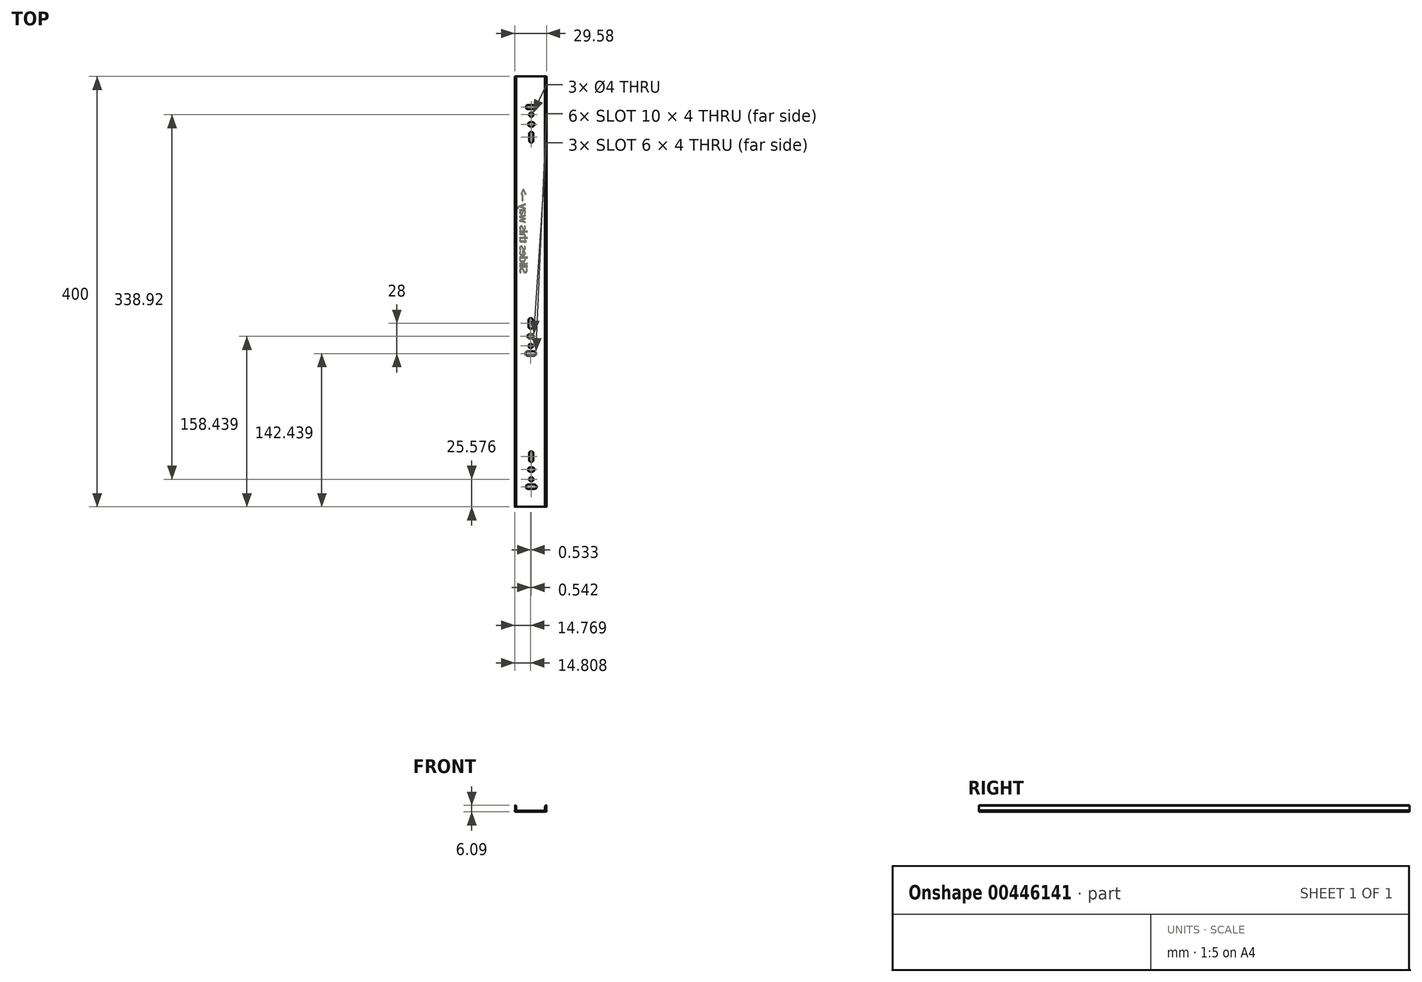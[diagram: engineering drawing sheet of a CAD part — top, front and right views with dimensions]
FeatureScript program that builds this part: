
annotation { "Feature Type Name" : "Feature", "Feature Type Description" : "" }
export const myFeature = defineFeature(function(context is Context, id is Id, definition is map)
    precondition{}
    {
        {
            var Q0;
            Q0=qCreatedBy(makeId("Front.planeOp"),FACE);
            var sketch = newSketch(context, id + "F0", { "sketchPlane" : qUnion([Q0])});
            skArc(sketch, "E0.filletArc", {"start": v(-14.79, 7.2) * mm, "mid": v(-14.47, 6.31) * mm, "end": v(-13.6, 5.94) * mm});
            skFitSpline(sketch, "E1", {"points": [v(-14.73, 11.64) * mm, v(-14.79, 7.2) * mm], "startDerivative": vector(1.38, -3.33) * mm, "endDerivative": vector(-2.04, -4.37) * mm});
            skFitSpline(sketch, "E2.MirrorCS", {"points": [v(14.73, 11.64) * mm, v(14.79, 7.2) * mm], "startDerivative": vector(-1.38, -3.33) * mm, "endDerivative": vector(2.04, -4.37) * mm});
            skArc(sketch, "E3.MirrorCS", {"start": v(14.79, 7.2) * mm, "mid": v(14.47, 6.31) * mm, "end": v(13.6, 5.94) * mm});
            skArc(sketch, "E4.1", {"start": v(-13.77, 7.04) * mm, "mid": v(-13.7, 6.97) * mm, "end": v(-13.6, 6.94) * mm});
            skFitSpline(sketch, "E4.2", {"points": [v(-13.8, 12.03) * mm, v(-13.66, 11.68) * mm, v(-13.43, 10.9) * mm, v(-13.29, 9.58) * mm, v(-13.39, 8.17) * mm, v(-13.67, 7.23) * mm, v(-13.88, 6.77) * mm]});
            skArc(sketch, "E5.1", {"start": v(13.77, 7.04) * mm, "mid": v(13.7, 6.97) * mm, "end": v(13.6, 6.94) * mm});
            skFitSpline(sketch, "E5.2", {"points": [v(13.8, 12.03) * mm, v(13.66, 11.68) * mm, v(13.43, 10.9) * mm, v(13.29, 9.58) * mm, v(13.39, 8.17) * mm, v(13.67, 7.23) * mm, v(13.88, 6.77) * mm]});
            skLineSegment(sketch, "E6", {"start": v(-13.8, 12.03) * mm, "end": v(-14.73, 11.64) * mm});
            skLineSegment(sketch, "E7", {"start": v(13.8, 12.03) * mm, "end": v(14.73, 11.64) * mm});
            skLineSegment(sketch, "E8", {"start": v(-13.6, 6.94) * mm, "end": v(13.6, 6.94) * mm});
            skLineSegment(sketch, "E9", {"start": v(13.6, 5.94) * mm, "end": v(-13.6, 5.94) * mm});
            skSolve(sketch);
        }
        {
            var Q0;
            Q0=makeQuery(id+"F0.imprint","IMPRINT",FACE,{"disambiguationData":[TD([[makeQuery(id+"F0.imprint","IMPRINT",EDGE,{"derivedFrom":sQuery(id+"F0.wireOp",EDGE,"E0.filletArc")}),1.0]])]});
            extrude(context, id + "F1", {"entities" : qUnion([Q0]), "endBound" : BoundingType.SYMMETRIC, "depth" : 400 * mm});
        }
        {
            var Q0;
            Q0=qCreatedBy(makeId("Top.planeOp"),FACE);
            var sketch = newSketch(context, id + "F2", { "sketchPlane" : qUnion([Q0])});
            skLineSegment(sketch, "E10.bottom", {"start": v(3.52, -183.42) * mm, "end": v(-2.48, -183.42) * mm});
            skLineSegment(sketch, "E10.top", {"start": v(3.52, -179.42) * mm, "end": v(-2.48, -179.42) * mm});
            skLineSegment(sketch, "E11.bottom", {"start": v(1.52, -167.42) * mm, "end": v(-0.48, -167.42) * mm});
            skLineSegment(sketch, "E11.top", {"start": v(1.52, -163.42) * mm, "end": v(-0.48, -163.42) * mm});
            skLineSegment(sketch, "E12.left", {"start": v(2.52, -156.42) * mm, "end": v(2.52, -150.42) * mm});
            skLineSegment(sketch, "E12.right", {"start": v(-1.48, -156.42) * mm, "end": v(-1.48, -150.42) * mm});
            skPoint(sketch, "E13.visualSharp", {"position": v(5.52, -183.42) * mm});
            skArc(sketch, "E13.filletArc", {"start": v(3.52, -183.42) * mm, "mid": v(4.94, -182.84) * mm, "end": v(5.52, -181.42) * mm});
            skPoint(sketch, "E14.visualSharp", {"position": v(5.52, -179.42) * mm});
            skArc(sketch, "E14.filletArc", {"start": v(5.52, -181.42) * mm, "mid": v(4.94, -180) * mm, "end": v(3.52, -179.42) * mm});
            skPoint(sketch, "E15.visualSharp", {"position": v(-4.48, -183.42) * mm});
            skArc(sketch, "E15.filletArc", {"start": v(-4.48, -181.42) * mm, "mid": v(-3.9, -182.84) * mm, "end": v(-2.48, -183.42) * mm});
            skPoint(sketch, "E16.visualSharp", {"position": v(-4.48, -179.42) * mm});
            skArc(sketch, "E16.filletArc", {"start": v(-2.48, -179.42) * mm, "mid": v(-3.9, -180) * mm, "end": v(-4.48, -181.42) * mm});
            skPoint(sketch, "E17.visualSharp", {"position": v(-1.48, -176.42) * mm});
            skArc(sketch, "E17.filletArc", {"start": v(-1.48, -174.42) * mm, "mid": v(-0.9, -175.84) * mm, "end": v(0.52, -176.42) * mm});
            skPoint(sketch, "E18.visualSharp", {"position": v(2.52, -176.42) * mm});
            skArc(sketch, "E18.filletArc", {"start": v(0.52, -176.42) * mm, "mid": v(1.94, -175.84) * mm, "end": v(2.52, -174.42) * mm});
            skPoint(sketch, "E19.visualSharp", {"position": v(2.52, -172.42) * mm});
            skArc(sketch, "E19.filletArc", {"start": v(2.52, -174.42) * mm, "mid": v(1.94, -173) * mm, "end": v(0.52, -172.42) * mm});
            skPoint(sketch, "E20.visualSharp", {"position": v(-1.48, -172.42) * mm});
            skArc(sketch, "E20.filletArc", {"start": v(0.52, -172.42) * mm, "mid": v(-0.9, -173) * mm, "end": v(-1.48, -174.42) * mm});
            skPoint(sketch, "E21.visualSharp", {"position": v(3.52, -167.42) * mm});
            skArc(sketch, "E21.filletArc", {"start": v(1.52, -167.42) * mm, "mid": v(2.94, -166.84) * mm, "end": v(3.52, -165.42) * mm});
            skPoint(sketch, "E22.visualSharp", {"position": v(3.52, -163.42) * mm});
            skArc(sketch, "E22.filletArc", {"start": v(3.52, -165.42) * mm, "mid": v(2.94, -164) * mm, "end": v(1.52, -163.42) * mm});
            skPoint(sketch, "E23.visualSharp", {"position": v(-2.48, -167.42) * mm});
            skArc(sketch, "E23.filletArc", {"start": v(-2.48, -165.42) * mm, "mid": v(-1.9, -166.84) * mm, "end": v(-0.48, -167.42) * mm});
            skPoint(sketch, "E24.visualSharp", {"position": v(-2.48, -163.42) * mm});
            skArc(sketch, "E24.filletArc", {"start": v(-0.48, -163.42) * mm, "mid": v(-1.9, -164) * mm, "end": v(-2.48, -165.42) * mm});
            skPoint(sketch, "E25.visualSharp", {"position": v(2.52, -158.42) * mm});
            skArc(sketch, "E25.filletArc", {"start": v(0.52, -158.42) * mm, "mid": v(1.94, -157.84) * mm, "end": v(2.52, -156.42) * mm});
            skPoint(sketch, "E26.visualSharp", {"position": v(-1.48, -158.42) * mm});
            skArc(sketch, "E26.filletArc", {"start": v(-1.48, -156.42) * mm, "mid": v(-0.9, -157.84) * mm, "end": v(0.52, -158.42) * mm});
            skPoint(sketch, "E27.visualSharp", {"position": v(2.52, -148.42) * mm});
            skArc(sketch, "E27.filletArc", {"start": v(2.52, -150.42) * mm, "mid": v(1.94, -149) * mm, "end": v(0.52, -148.42) * mm});
            skPoint(sketch, "E28.visualSharp", {"position": v(-1.48, -148.42) * mm});
            skArc(sketch, "E28.filletArc", {"start": v(0.52, -148.42) * mm, "mid": v(-0.9, -149) * mm, "end": v(-1.48, -150.42) * mm});
            skLineSegment(sketch, "E29.bottom", {"start": v(3.02, -59.56) * mm, "end": v(-2.98, -59.56) * mm});
            skLineSegment(sketch, "E29.top", {"start": v(3.02, -55.56) * mm, "end": v(-2.98, -55.56) * mm});
            skPoint(sketch, "E30.visualSharp", {"position": v(5.02, -59.56) * mm});
            skArc(sketch, "E30.filletArc", {"start": v(3.02, -59.56) * mm, "mid": v(4.43, -58.98) * mm, "end": v(5.02, -57.56) * mm});
            skPoint(sketch, "E31.visualSharp", {"position": v(5.02, -55.56) * mm});
            skArc(sketch, "E31.filletArc", {"start": v(5.02, -57.56) * mm, "mid": v(4.43, -56.15) * mm, "end": v(3.02, -55.56) * mm});
            skPoint(sketch, "E32.visualSharp", {"position": v(-4.98, -55.56) * mm});
            skArc(sketch, "E32.filletArc", {"start": v(-2.98, -55.56) * mm, "mid": v(-4.4, -56.15) * mm, "end": v(-4.98, -57.56) * mm});
            skPoint(sketch, "E33.visualSharp", {"position": v(-4.98, -59.56) * mm});
            skArc(sketch, "E33.filletArc", {"start": v(-4.98, -57.56) * mm, "mid": v(-4.4, -58.98) * mm, "end": v(-2.98, -59.56) * mm});
            skCircle(sketch, "E34", {"center": v(0.02, -50.56) * mm, "radius": 2 * mm});
            skPoint(sketch, "E35", {"position": v(0.02, -55.56) * mm});
            skLineSegment(sketch, "E36.bottom", {"start": v(0.98, -43.56) * mm, "end": v(-1.02, -43.56) * mm});
            skLineSegment(sketch, "E36.top", {"start": v(0.98, -39.56) * mm, "end": v(-1.02, -39.56) * mm});
            skPoint(sketch, "E37.visualSharp", {"position": v(2.98, -43.56) * mm});
            skArc(sketch, "E37.filletArc", {"start": v(0.98, -43.56) * mm, "mid": v(2.4, -42.98) * mm, "end": v(2.98, -41.56) * mm});
            skPoint(sketch, "E38.visualSharp", {"position": v(2.98, -39.56) * mm});
            skArc(sketch, "E38.filletArc", {"start": v(2.98, -41.56) * mm, "mid": v(2.4, -40.15) * mm, "end": v(0.98, -39.56) * mm});
            skPoint(sketch, "E39.visualSharp", {"position": v(-3.02, -39.56) * mm});
            skArc(sketch, "E39.filletArc", {"start": v(-1.02, -39.56) * mm, "mid": v(-2.44, -40.15) * mm, "end": v(-3.02, -41.56) * mm});
            skPoint(sketch, "E40.visualSharp", {"position": v(-3.02, -43.56) * mm});
            skArc(sketch, "E40.filletArc", {"start": v(-3.02, -41.56) * mm, "mid": v(-2.44, -42.98) * mm, "end": v(-1.02, -43.56) * mm});
            skLineSegment(sketch, "E41.left", {"start": v(2.02, -32.56) * mm, "end": v(2.02, -26.56) * mm});
            skLineSegment(sketch, "E41.right", {"start": v(-1.98, -32.56) * mm, "end": v(-1.98, -26.56) * mm});
            skPoint(sketch, "E42.visualSharp", {"position": v(2.02, -34.56) * mm});
            skArc(sketch, "E42.filletArc", {"start": v(0.02, -34.56) * mm, "mid": v(1.43, -33.98) * mm, "end": v(2.02, -32.56) * mm});
            skPoint(sketch, "E43.visualSharp", {"position": v(-1.98, -34.56) * mm});
            skArc(sketch, "E43.filletArc", {"start": v(-1.98, -32.56) * mm, "mid": v(-1.4, -33.98) * mm, "end": v(0.02, -34.56) * mm});
            skPoint(sketch, "E44.visualSharp", {"position": v(2.02, -24.56) * mm});
            skArc(sketch, "E44.filletArc", {"start": v(2.02, -26.56) * mm, "mid": v(1.43, -25.15) * mm, "end": v(0.02, -24.56) * mm});
            skPoint(sketch, "E45.visualSharp", {"position": v(-1.98, -24.56) * mm});
            skArc(sketch, "E45.filletArc", {"start": v(0.02, -24.56) * mm, "mid": v(-1.4, -25.15) * mm, "end": v(-1.98, -26.56) * mm});
            skLineSegment(sketch, "E46.bottom", {"start": v(-2.45, 173.5) * mm, "end": v(3.55, 173.5) * mm});
            skLineSegment(sketch, "E46.top", {"start": v(-2.45, 169.5) * mm, "end": v(3.55, 169.5) * mm});
            skPoint(sketch, "E47.visualSharp", {"position": v(-4.45, 173.5) * mm});
            skArc(sketch, "E47.filletArc", {"start": v(-2.45, 173.5) * mm, "mid": v(-3.86, 172.91) * mm, "end": v(-4.45, 171.5) * mm});
            skPoint(sketch, "E48.visualSharp", {"position": v(-4.45, 169.5) * mm});
            skArc(sketch, "E48.filletArc", {"start": v(-4.45, 171.5) * mm, "mid": v(-3.86, 170.08) * mm, "end": v(-2.45, 169.5) * mm});
            skPoint(sketch, "E49.visualSharp", {"position": v(5.55, 169.5) * mm});
            skArc(sketch, "E49.filletArc", {"start": v(3.55, 169.5) * mm, "mid": v(4.97, 170.08) * mm, "end": v(5.55, 171.5) * mm});
            skPoint(sketch, "E50.visualSharp", {"position": v(5.55, 173.5) * mm});
            skArc(sketch, "E50.filletArc", {"start": v(5.55, 171.5) * mm, "mid": v(4.97, 172.91) * mm, "end": v(3.55, 173.5) * mm});
            skCircle(sketch, "E51", {"center": v(0.55, 164.5) * mm, "radius": 2 * mm});
            skPoint(sketch, "E52", {"position": v(0.55, 169.5) * mm});
            skLineSegment(sketch, "E53.bottom", {"start": v(-0.4, 157.5) * mm, "end": v(1.6, 157.5) * mm});
            skLineSegment(sketch, "E53.top", {"start": v(-0.4, 153.5) * mm, "end": v(1.6, 153.5) * mm});
            skPoint(sketch, "E54.visualSharp", {"position": v(-2.4, 157.5) * mm});
            skArc(sketch, "E54.filletArc", {"start": v(-0.4, 157.5) * mm, "mid": v(-1.82, 156.91) * mm, "end": v(-2.4, 155.5) * mm});
            skPoint(sketch, "E55.visualSharp", {"position": v(-2.4, 153.5) * mm});
            skArc(sketch, "E55.filletArc", {"start": v(-2.4, 155.5) * mm, "mid": v(-1.82, 154.08) * mm, "end": v(-0.4, 153.5) * mm});
            skPoint(sketch, "E56.visualSharp", {"position": v(3.6, 153.5) * mm});
            skArc(sketch, "E56.filletArc", {"start": v(1.6, 153.5) * mm, "mid": v(3, 154.08) * mm, "end": v(3.6, 155.5) * mm});
            skPoint(sketch, "E57.visualSharp", {"position": v(3.6, 157.5) * mm});
            skArc(sketch, "E57.filletArc", {"start": v(3.6, 155.5) * mm, "mid": v(3, 156.91) * mm, "end": v(1.6, 157.5) * mm});
            skLineSegment(sketch, "E58.left", {"start": v(-1.45, 146.5) * mm, "end": v(-1.45, 140.5) * mm});
            skLineSegment(sketch, "E58.right", {"start": v(2.55, 146.5) * mm, "end": v(2.55, 140.5) * mm});
            skPoint(sketch, "E59.visualSharp", {"position": v(-1.45, 148.5) * mm});
            skArc(sketch, "E59.filletArc", {"start": v(0.55, 148.5) * mm, "mid": v(-0.86, 147.91) * mm, "end": v(-1.45, 146.5) * mm});
            skPoint(sketch, "E60.visualSharp", {"position": v(2.55, 148.5) * mm});
            skArc(sketch, "E60.filletArc", {"start": v(2.55, 146.5) * mm, "mid": v(1.97, 147.91) * mm, "end": v(0.55, 148.5) * mm});
            skPoint(sketch, "E61.visualSharp", {"position": v(-1.45, 138.5) * mm});
            skArc(sketch, "E61.filletArc", {"start": v(-1.45, 140.5) * mm, "mid": v(-0.86, 139.08) * mm, "end": v(0.55, 138.5) * mm});
            skPoint(sketch, "E62.visualSharp", {"position": v(2.55, 138.5) * mm});
            skArc(sketch, "E62.filletArc", {"start": v(0.55, 138.5) * mm, "mid": v(1.97, 139.08) * mm, "end": v(2.55, 140.5) * mm});
            skSolve(sketch);
        }
        {
            var Q0;
            Q0=makeQuery(id+"F2.imprint","IMPRINT",FACE,{"disambiguationData":[TD([[makeQuery(id+"F2.imprint","IMPRINT",EDGE,{"derivedFrom":sQuery(id+"F2.wireOp",EDGE,"E29.bottom")}),-1.0]])]});
            var Q1;
            Q1=makeQuery(id+"F2.imprint","IMPRINT",FACE,{"disambiguationData":[TD([[makeQuery(id+"F2.imprint","IMPRINT",EDGE,{"derivedFrom":sQuery(id+"F2.wireOp",EDGE,"E34")}),1.0]])]});
            var Q2;
            Q2=makeQuery(id+"F2.imprint","IMPRINT",FACE,{"disambiguationData":[TD([[makeQuery(id+"F2.imprint","IMPRINT",EDGE,{"derivedFrom":sQuery(id+"F2.wireOp",EDGE,"E36.bottom")}),-1.0]])]});
            var Q3;
            Q3=makeQuery(id+"F2.imprint","IMPRINT",FACE,{"disambiguationData":[TD([[makeQuery(id+"F2.imprint","IMPRINT",EDGE,{"derivedFrom":sQuery(id+"F2.wireOp",EDGE,"E41.left")}),1.0]])]});
            var Q4;
            Q4=makeQuery(id+"F2.imprint","IMPRINT",FACE,{"disambiguationData":[TD([[makeQuery(id+"F2.imprint","IMPRINT",EDGE,{"derivedFrom":sQuery(id+"F2.wireOp",EDGE,"E12.left")}),1.0]])]});
            var Q5;
            Q5=makeQuery(id+"F2.imprint","IMPRINT",FACE,{"disambiguationData":[TD([[makeQuery(id+"F2.imprint","IMPRINT",EDGE,{"derivedFrom":sQuery(id+"F2.wireOp",EDGE,"E11.bottom")}),-1.0]])]});
            var Q6;
            Q6=makeQuery(id+"F2.imprint","IMPRINT",FACE,{"disambiguationData":[TD([[makeQuery(id+"F2.imprint","IMPRINT",EDGE,{"derivedFrom":sQuery(id+"F2.wireOp",EDGE,"E17.filletArc")}),1.0]])]});
            var Q7;
            Q7=makeQuery(id+"F2.imprint","IMPRINT",FACE,{"disambiguationData":[TD([[makeQuery(id+"F2.imprint","IMPRINT",EDGE,{"derivedFrom":sQuery(id+"F2.wireOp",EDGE,"E10.bottom")}),-1.0]])]});
            var Q8;
            Q8=makeQuery(id+"F2.imprint","IMPRINT",FACE,{"disambiguationData":[TD([[makeQuery(id+"F2.imprint","IMPRINT",EDGE,{"derivedFrom":sQuery(id+"F2.wireOp",EDGE,"E58.left")}),1.0]])]});
            var Q9;
            Q9=makeQuery(id+"F2.imprint","IMPRINT",FACE,{"disambiguationData":[TD([[makeQuery(id+"F2.imprint","IMPRINT",EDGE,{"derivedFrom":sQuery(id+"F2.wireOp",EDGE,"E53.bottom")}),-1.0]])]});
            var Q10;
            Q10=makeQuery(id+"F2.imprint","IMPRINT",FACE,{"disambiguationData":[TD([[makeQuery(id+"F2.imprint","IMPRINT",EDGE,{"derivedFrom":sQuery(id+"F2.wireOp",EDGE,"E51")}),1.0]])]});
            var Q11;
            Q11=makeQuery(id+"F2.imprint","IMPRINT",FACE,{"disambiguationData":[TD([[makeQuery(id+"F2.imprint","IMPRINT",EDGE,{"derivedFrom":sQuery(id+"F2.wireOp",EDGE,"E46.bottom")}),-1.0]])]});
            extrude(context, id + "F3", {"entities" : qUnion([Q0, Q1, Q2, Q3, Q4, Q5, Q6, Q7, Q8, Q9, Q10, Q11]), "operationType" : NewBodyOperationType.REMOVE, "endBound" : BoundingType.THROUGH_ALL, "depth" : 25 * mm});
        }
        {
            var Q0;
            Q0=qCreatedBy(makeId("Top.planeOp"),FACE);
            var sketch = newSketch(context, id + "F4", { "sketchPlane" : qUnion([Q0])});
            skText(sketch, "E63", { "text": "Slides this way -->", "fontName": "OpenSans-Bold.ttf"});
            const initialGuessF4  = {"E63": [0.0046, 0.00687, 0, 1, 0.008]};
            skSetInitialGuess(sketch, initialGuessF4);
            skSolve(sketch);
        }
        {
            var Q0;
            {var subQ0=sQuery(id+"F0.wireOp",EDGE,"E9");var subQ11=sQuery(id+"F0.wireOp",EDGE,"E0.filletArc");Q0=makeQuery(id+"FNEuVr31Iejyk5I_1.boolean.opBoolean","SPLIT",FACE,{"disambiguationData":[TD([makeQuery(id+"F1.opExtrude","SWEPT_FACE",FACE,{"disambiguationData":[OSD([subQ11])]})])],"derivedFrom":makeQuery(id+"F1.opExtrude","SWEPT_FACE",FACE,{"disambiguationData":[OSD([subQ0])]})});}
            var sketch = newSketch(context, id + "F5", { "sketchPlane" : qUnion([Q0])});
            skText(sketch, "E64", { "text": "Slides this way -->", "fontName": "OpenSans-Regular.ttf"});
            skPoint(sketch, "E64.secondSnap0", {"position": v(-2.4, -155.5) * mm});
            const initialGuessF5  = {"E64": [-0.01012, -0.01695, 0, -1, 0.00688]};
            skSetInitialGuess(sketch, initialGuessF5);
            skSolve(sketch);
        }
        {
            var Q0;
            Q0=qSketchRegion(id+"F5",true);
            extrude(context, id + "F6", {"entities" : qUnion([Q0]), "operationType" : NewBodyOperationType.REMOVE, "oppositeDirection" : true, "depth" : .4 * mm});
        }
    });
